# Revit family: Legrand_Practibox³_18_módulos_puerta_transparente
name_source: partatom
category: Equipement électrique
revit_build: Autodesk Revit 2018 (Build: 20170223_1515(x64)
units: mm (PartAtom-declared; Revit-internal decimal feet)

## family parameters
Basée sur le plan de construction = Non
Configuration du panneau = Deux colonnes, circuits au sein
Cote de connecteur circulaire = Utiliser le diamètre
Couper avec des vides une fois chargée = Non
Numéro OmniClass = 23.80.30.11.17
Partagée = Non
Point de calcul de pièce = Non
Titre OmniClass = Distribution Boards and Control Panels
Toujours verticalement = Oui
Type d'élément = Tableau de raccordement

## types (8) — shared parameters
Condiciones Generales de Uso = https://export.legrand.com
Fabricant = Legrand
Modèle = Practibox³
URL = www.legrand.com
anchura = 493 mm  [stored 1.61745 ft]

## per-type parameters (varying)
| type | 401706 | 401707 | 401708 | 401709 | 401756 | 401757 | 401758 | 401759 | Altura | Bornas N | Bornas T | profundidad |
| Practibox³ 1x18 módulos 401706 | Oui | Non | Non | Non | Non | Non | Non | Non | 288 mm  [stored 0.944882 ft] |  | terminal 13 hoyos | 105 mm  [stored 0.344488 ft] |
| Practibox³ 2x18 módulos 401707 | Non | Oui | Non | Non | Non | Non | Non | Non | 496 mm  [stored 1.6273 ft] |  | terminal 17 hoyos | 105 mm  [stored 0.344488 ft] |
| Practibox³ 3x18 módulos 401708 | Non | Non | Oui | Non | Non | Non | Non | Non | 650 mm  [stored 2.13255 ft] |  | terminal 22 hoyos | 111 mm |
| Practibox³ 4x18 módulos 401709 | Non | Non | Non | Oui | Non | Non | Non | Non | 800 mm  [stored 2.62467 ft] |  | terminal 35 hoyos | 111 mm |
| Practibox³ 1x18 módulos 401756 | Non | Non | Non | Non | Oui | Non | Non | Non | 288 mm  [stored 0.944882 ft] | terminal 13 hoyos | terminal 13 hoyos | 105 mm  [stored 0.344488 ft] |
| Practibox³ 2x18 módulos 401757 | Non | Non | Non | Non | Non | Oui | Non | Non | 496 mm  [stored 1.6273 ft] | terminal 2x8 hoyos | terminal 17 hoyos | 105 mm  [stored 0.344488 ft] |
| Practibox³ 3x18 módulos 401758 | Non | Non | Non | Non | Non | Non | Oui | Non | 650 mm  [stored 2.13255 ft] | terminal 3x8 hoyos | terminal 22 hoyos | 111 mm |
| Practibox³ 4x18 módulos 401759 | Non | Non | Non | Non | Non | Non | Non | Oui | 800 mm  [stored 2.62467 ft] | terminal 4x8 hoyos | terminal 35 hoyos | 111 mm |

note: [stored X ft] marks values corroborated as IEEE doubles in the binary element streams (Revit-internal decimal feet)
